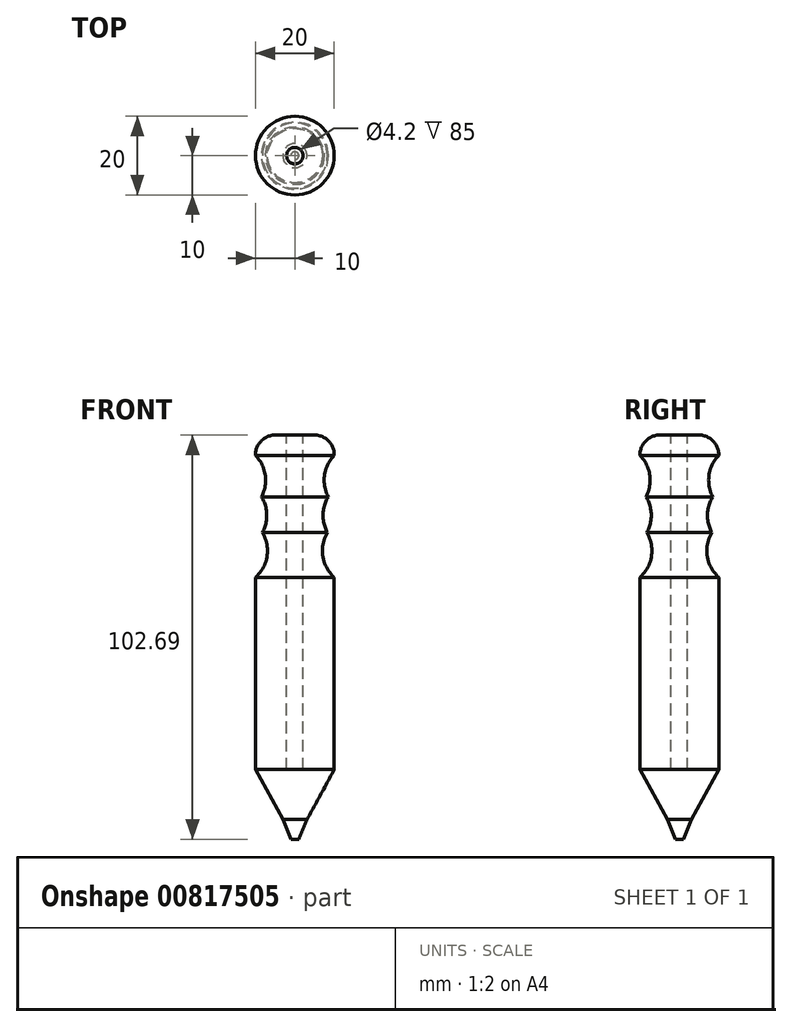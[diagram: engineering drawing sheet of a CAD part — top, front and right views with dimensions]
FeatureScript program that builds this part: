
annotation { "Feature Type Name" : "Feature", "Feature Type Description" : "" }
export const myFeature = defineFeature(function(context is Context, id is Id, definition is map)
    precondition{}
    {
        {
            var Q0;
            Q0=qCreatedBy(makeId("Front.planeOp"),FACE);
            var sketch = newSketch(context, id + "F0", { "sketchPlane" : qUnion([Q0])});
            skLineSegment(sketch, "E0", {"start": v(-1, 0) * mm, "end": v(-3.07, 5) * mm});
            skLineSegment(sketch, "E1", {"start": v(-3.07, 5) * mm, "end": v(-10, 17.7) * mm});
            skLineSegment(sketch, "E2", {"start": v(-10, 17.7) * mm, "end": v(-10, 66.57) * mm});
            skLineSegment(sketch, "E3", {"start": v(-10, 102.7) * mm, "end": v(-2.1, 102.7) * mm});
            skLineSegment(sketch, "E4", {"start": v(-2.1, 102.7) * mm, "end": v(-2.1, 17.7) * mm});
            skLineSegment(sketch, "E5", {"start": v(-2.1, 17.7) * mm, "end": v(0, 17.7) * mm});
            skArc(sketch, "E6", {"start": v(-16.25, 82.26) * mm, "mid": v(-16.18, 82.26) * mm, "end": v(-16.12, 82.27) * mm});
            skArc(sketch, "E7", {"start": v(-8.26, 77.92) * mm, "mid": v(-7.15, 82.5) * mm, "end": v(-8.5, 87) * mm});
            skArc(sketch, "E8", {"start": v(-10, 66.57) * mm, "mid": v(-7.08, 71.94) * mm, "end": v(-8.26, 77.92) * mm});
            skArc(sketch, "E9.trimOffspring", {"start": v(-8.5, 87) * mm, "mid": v(-7.53, 92.5) * mm, "end": v(-10, 97.51) * mm});
            skArc(sketch, "E10.trimOffspring", {"start": v(-16.12, 82.27) * mm, "mid": v(-16.18, 82.27) * mm, "end": v(-16.25, 82.26) * mm});
            skLineSegment(sketch, "E11.trimOffspring", {"start": v(-10, 97.51) * mm, "end": v(-10, 102.7) * mm});
            skLineSegment(sketch, "E12", {"start": v(0, 17.7) * mm, "end": v(0, 0) * mm});
            skLineSegment(sketch, "E13", {"start": v(0, 0) * mm, "end": v(-1, 0) * mm});
            skSolve(sketch);
        }
        {
            var Q0;
            Q0=makeQuery(id+"F0.imprint","IMPRINT",FACE,{"disambiguationData":[TD([[makeQuery(id+"F0.imprint","IMPRINT",EDGE,{"derivedFrom":sQuery(id+"F0.wireOp",EDGE,"E0")}),-1.0]])]});
            var Q1;
            Q1=sQuery(id+"F0.wireOp",EDGE,"E12");
            revolve(context, id + "F1", {"surfaceOperationType" : NewSurfaceOperationType.NEW, "entities" : qUnion([Q0]), "axis" : qUnion([Q1]), "revolveType" : RevolveType.FULL});
        }
        {
            var Q0;
            Q0=makeQuery(id+"F1.opRevolve","SWEPT_EDGE",EDGE,{"disambiguationData":[OSD([sQuery(id+"F0.wireOp",EDGE,"E3"),sQuery(id+"F0.wireOp",EDGE,"E11.trimOffspring")])]});
            fillet(context, id + "F2", {"entities" : qUnion([Q0]), "radius" : 5 * mm, "tangentPropagation" : true, "allowEdgeOverflow" : false});
        }
    });
